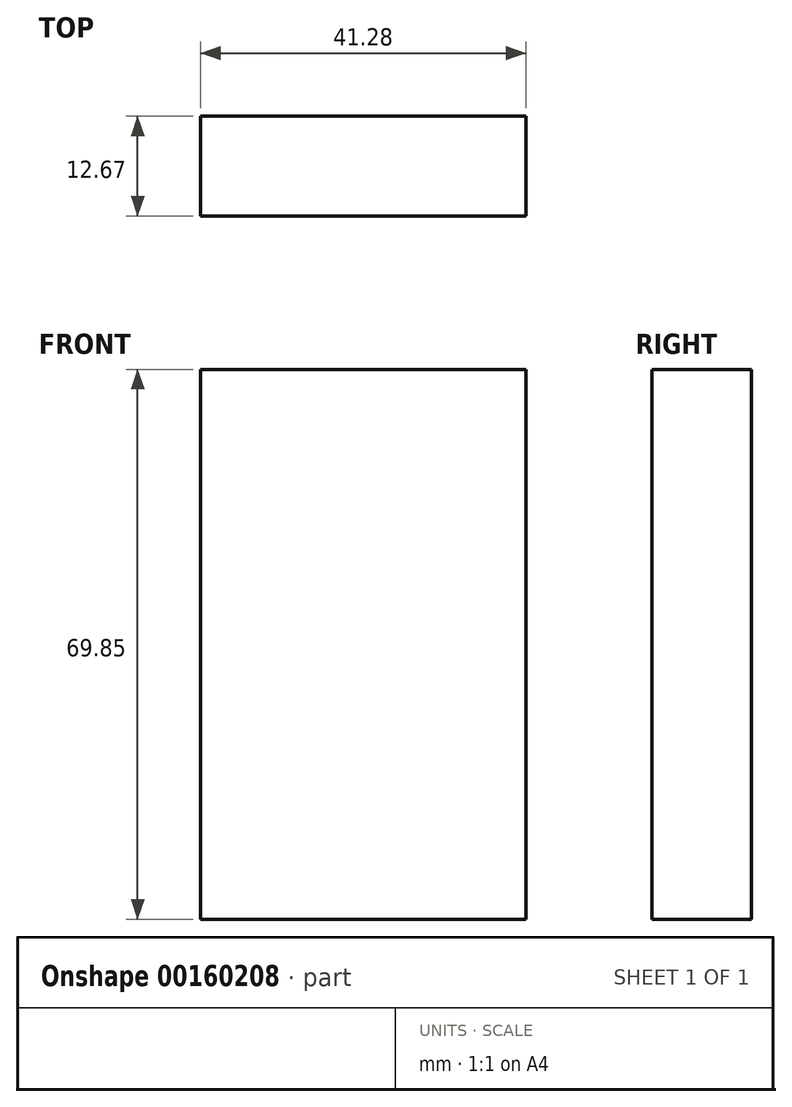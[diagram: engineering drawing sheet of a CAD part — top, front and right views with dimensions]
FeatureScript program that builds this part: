
annotation { "Feature Type Name" : "Feature", "Feature Type Description" : "" }
export const myFeature = defineFeature(function(context is Context, id is Id, definition is map)
    precondition{}
    {
        {
            var Q0;
            Q0=qCreatedBy(makeId("Top.planeOp"),FACE);
            var sketch = newSketch(context, id + "F0", { "sketchPlane" : qUnion([Q0])});
            skLineSegment(sketch, "E0.bottom", {"start": v(0, 0) * mm, "end": v(41.28, 0) * mm});
            skLineSegment(sketch, "E0.top", {"start": v(0, 12.67) * mm, "end": v(41.28, 12.67) * mm});
            skLineSegment(sketch, "E0.left", {"start": v(0, 0) * mm, "end": v(0, 12.67) * mm});
            skLineSegment(sketch, "E0.right", {"start": v(41.28, 0) * mm, "end": v(41.28, 12.67) * mm});
            skSolve(sketch);
        }
        {
            var Q0;
            Q0=sQuery(id+"F0.wireOp",EDGE,"E0.right");
            var Q1;
            Q1=sQuery(id+"F0.wireOp",EDGE,"E0.left");
            var Q2;
            Q2=sQuery(id+"F0.wireOp",EDGE,"E0.top");
            var Q3;
            Q3=sQuery(id+"F0.wireOp",EDGE,"E0.bottom");
            extrude(context, id + "F1", {"bodyType" : ToolBodyType.SURFACE, "surfaceEntities" : qUnion([Q0, Q1, Q2, Q3]), "depth" : 69.85 * mm});
        }
    });
